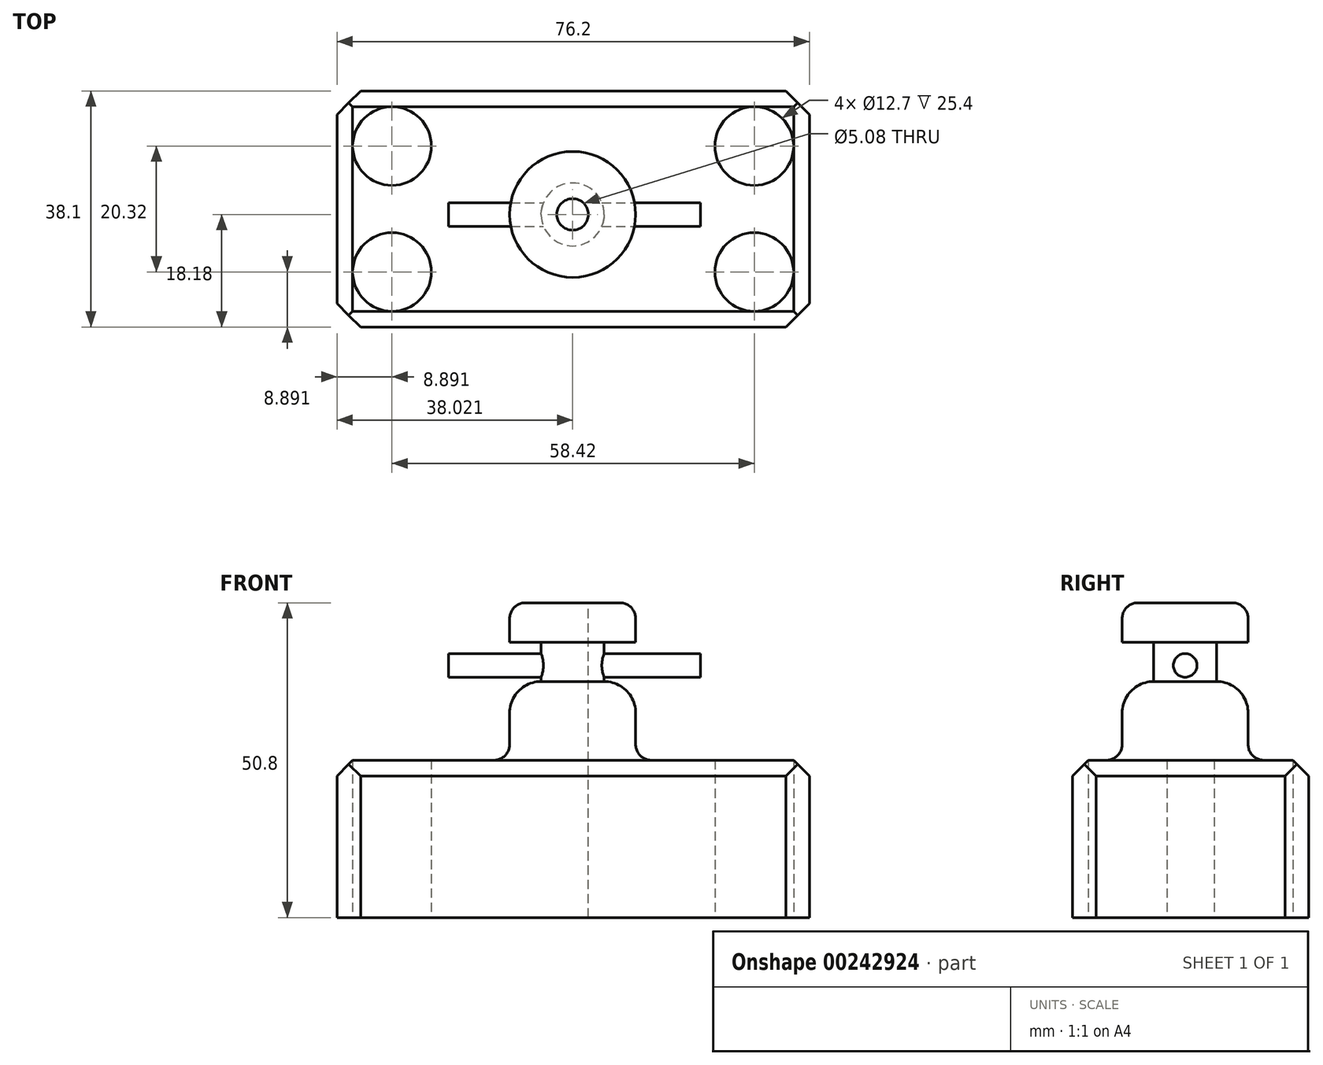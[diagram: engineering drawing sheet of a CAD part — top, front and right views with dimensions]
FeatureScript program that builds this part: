
annotation { "Feature Type Name" : "Feature", "Feature Type Description" : "" }
export const myFeature = defineFeature(function(context is Context, id is Id, definition is map)
    precondition{}
    {
        {
            var Q0;
            Q0=qCreatedBy(makeId("Top.planeOp"),FACE);
            var sketch = newSketch(context, id + "F0", { "sketchPlane" : qUnion([Q0])});
            skLineSegment(sketch, "E0.bottom", {"start": v(-43.42, 19.92) * mm, "end": v(32.78, 19.92) * mm});
            skLineSegment(sketch, "E0.top", {"start": v(-43.42, -18.18) * mm, "end": v(32.78, -18.18) * mm});
            skLineSegment(sketch, "E0.left", {"start": v(-43.42, 19.92) * mm, "end": v(-43.42, -18.18) * mm});
            skLineSegment(sketch, "E0.right", {"start": v(32.78, 19.92) * mm, "end": v(32.78, -18.18) * mm});
            skSolve(sketch);
        }
        {
            var Q0;
            Q0=makeQuery(id+"F0.imprint","IMPRINT",FACE,{"disambiguationData":[TD([[makeQuery(id+"F0.imprint","IMPRINT",EDGE,{"derivedFrom":sQuery(id+"F0.wireOp",EDGE,"E0.bottom")}),-1.0]])]});
            extrude(context, id + "F1", {"entities" : qUnion([Q0]), "depth" : 25.4 * mm});
        }
        {
            var Q0;
            Q0=qCreatedBy(makeId("Top.planeOp"),FACE);
            var sketch = newSketch(context, id + "F2", { "sketchPlane" : qUnion([Q0])});
            skCircle(sketch, "E1", {"center": v(-34.53, -9.29) * mm, "radius": 6.35 * mm});
            skCircle(sketch, "E2", {"center": v(23.9, 11.03) * mm, "radius": 6.35 * mm});
            skCircle(sketch, "E3", {"center": v(23.9, -9.29) * mm, "radius": 6.35 * mm});
            skCircle(sketch, "E4", {"center": v(-34.53, 11.03) * mm, "radius": 6.35 * mm});
            skSolve(sketch);
        }
        {
            var Q0;
            Q0 = qSketchRegion(id + "F2", true);
            var Q1;
            Q1=makeQuery(id+"F1.opExtrude","CAP_FACE",FACE,{"disambiguationData":[OSD([sQuery(id+"F0.wireOp",EDGE,"E0.bottom"),sQuery(id+"F0.wireOp",EDGE,"E0.top"),sQuery(id+"F0.wireOp",EDGE,"E0.left"),sQuery(id+"F0.wireOp",EDGE,"E0.right")])],"isStart":false});
            extrude(context, id + "F3", {"entities" : qUnion([Q0, Q1]), "operationType" : NewBodyOperationType.REMOVE, "depth" : 25.4 * mm});
        }
        {
            var Q0;
            Q0=makeQuery(id+"F1.opExtrude","CAP_EDGE",EDGE,{"disambiguationData":[OSD([sQuery(id+"F0.wireOp",EDGE,"E0.top")])],"isStart":false});
            var Q1;
            Q1=makeQuery(id+"F1.opExtrude","CAP_EDGE",EDGE,{"disambiguationData":[OSD([sQuery(id+"F0.wireOp",EDGE,"E0.right")])],"isStart":false});
            var Q2;
            Q2=makeQuery(id+"F1.opExtrude","CAP_EDGE",EDGE,{"disambiguationData":[OSD([sQuery(id+"F0.wireOp",EDGE,"E0.bottom")])],"isStart":false});
            var Q3;
            Q3=makeQuery(id+"F1.opExtrude","CAP_EDGE",EDGE,{"disambiguationData":[OSD([sQuery(id+"F0.wireOp",EDGE,"E0.left")])],"isStart":false});
            chamfer(context, id + "F4", {"entities" : qUnion([Q0, Q1, Q2, Q3]), "width" : 2.54 * mm, "tangentPropagation" : true});
        }
        {
            var Q0;
            Q0=qCreatedBy(makeId("Top.planeOp"),FACE);
            var sketch = newSketch(context, id + "F5", { "sketchPlane" : qUnion([Q0])});
            skLineSegment(sketch, "E5", {"start": v(32.7, 0) * mm, "end": v(-5.4, 0) * mm});
            skCircle(sketch, "E6", {"center": v(-5.4, 0) * mm, "radius": 10.16 * mm});
            skSolve(sketch);
        }
        {
            var Q0;
            Q0 = qSketchRegion(id + "F5", true);
            extrude(context, id + "F6", {"entities" : qUnion([Q0]), "operationType" : NewBodyOperationType.ADD, "depth" : 38.1 * mm});
        }
        {
            var Q0;
            Q0=makeQuery(id+"F6.opExtrude","CAP_FACE",FACE,{"disambiguationData":[OSD([sQuery(id+"F5.wireOp",EDGE,"E6")])],"isStart":false});
            var sketch = newSketch(context, id + "F7", { "sketchPlane" : qUnion([Q0])});
            skCircle(sketch, "E7", {"center": v(-5.4, 0) * mm, "radius": 5.08 * mm});
            skSolve(sketch);
        }
        {
            var Q0;
            Q0 = qSketchRegion(id + "F7", true);
            extrude(context, id + "F8", {"entities" : qUnion([Q0]), "operationType" : NewBodyOperationType.ADD, "depth" : 6.35 * mm});
        }
        {
            var Q0;
            Q0=makeQuery(id+"F8.opExtrude","CAP_FACE",FACE,{"disambiguationData":[OSD([sQuery(id+"F7.wireOp",EDGE,"E7")])],"isStart":false});
            var sketch = newSketch(context, id + "F9", { "sketchPlane" : qUnion([Q0])});
            skCircle(sketch, "E8", {"center": v(-5.4, 0) * mm, "radius": 10.16 * mm});
            skSolve(sketch);
        }
        {
            var Q0;
            Q0 = qSketchRegion(id + "F9", true);
            extrude(context, id + "F10", {"entities" : qUnion([Q0]), "operationType" : NewBodyOperationType.ADD, "depth" : 6.35 * mm});
        }
        {
            var Q0;
            Q0=qCreatedBy(makeId("Right.planeOp"),FACE);
            var sketch = newSketch(context, id + "F11", { "sketchPlane" : qUnion([Q0])});
            skCircle(sketch, "E9", {"center": v(0, 40.7) * mm, "radius": 1.9 * mm});
            skSolve(sketch);
        }
        {
            var Q0;
            Q0 = qSketchRegion(id + "F11", true);
            extrude(context, id + "F12", {"entities" : qUnion([Q0]), "operationType" : NewBodyOperationType.ADD, "oppositeDirection" : true, "depth" : 25.4 * mm});
        }
        {
            var Q0;
            Q0 = qSketchRegion(id + "F11", true);
            extrude(context, id + "F13", {"entities" : qUnion([Q0]), "operationType" : NewBodyOperationType.ADD, "depth" : 15.24 * mm});
        }
        {
            var Q0;
            Q0=makeQuery(id+"F6.boolean.opBoolean","INTERSECT",EDGE,{"derivedFrom":[makeQuery(id+"F4.opChamfer","SPLIT",FACE,{"disambiguationData":[OD(4.0)],"derivedFrom":makeQuery(id+"F1.opExtrude","CAP_FACE",FACE,{"disambiguationData":[OSD([sQuery(id+"F0.wireOp",EDGE,"E0.bottom"),sQuery(id+"F0.wireOp",EDGE,"E0.top"),sQuery(id+"F0.wireOp",EDGE,"E0.left"),sQuery(id+"F0.wireOp",EDGE,"E0.right")])],"isStart":false})}),makeQuery(id+"F6.opExtrude","SWEPT_FACE",FACE,{"disambiguationData":[OSD([sQuery(id+"F5.wireOp",EDGE,"E6")])]})]});
            fillet(context, id + "F14", {"entities" : qUnion([Q0]), "radius" : 2.54 * mm, "tangentPropagation" : true, "allowEdgeOverflow" : false});
        }
        {
            var Q0;
            Q0=makeQuery(id+"F10.opExtrude","CAP_EDGE",EDGE,{"disambiguationData":[OSD([sQuery(id+"F9.wireOp",EDGE,"E8")])],"isStart":false});
            fillet(context, id + "F15", {"entities" : qUnion([Q0]), "radius" : 2.54 * mm, "tangentPropagation" : true, "allowEdgeOverflow" : false});
        }
        {
            var Q0;
            Q0=makeQuery(id+"F10.opExtrude","CAP_FACE",FACE,{"disambiguationData":[OSD([sQuery(id+"F9.wireOp",EDGE,"E8")])],"isStart":false});
            var sketch = newSketch(context, id + "F16", { "sketchPlane" : qUnion([Q0])});
            skCircle(sketch, "E10", {"center": v(-5.4, 0) * mm, "radius": 2.54 * mm});
            skSolve(sketch);
        }
        {
            var Q0;
            Q0 = qSketchRegion(id + "F16", true);
            extrude(context, id + "F17", {"entities" : qUnion([Q0]), "operationType" : NewBodyOperationType.REMOVE, "oppositeDirection" : true, "depth" : 50.8 * mm});
        }
        {
            var Q0;
            Q0=makeQuery(id+"F1.opExtrude","SWEPT_EDGE",EDGE,{"disambiguationData":[OSD([sQuery(id+"F0.wireOp",EDGE,"E0.top"),sQuery(id+"F0.wireOp",EDGE,"E0.right")])]});
            var Q1;
            Q1=makeQuery(id+"F1.opExtrude","SWEPT_EDGE",EDGE,{"disambiguationData":[OSD([sQuery(id+"F0.wireOp",EDGE,"E0.top"),sQuery(id+"F0.wireOp",EDGE,"E0.left")])]});
            var Q2;
            Q2=makeQuery(id+"F1.opExtrude","SWEPT_EDGE",EDGE,{"disambiguationData":[OSD([sQuery(id+"F0.wireOp",EDGE,"E0.bottom"),sQuery(id+"F0.wireOp",EDGE,"E0.right")])]});
            var Q3;
            Q3=makeQuery(id+"F1.opExtrude","SWEPT_EDGE",EDGE,{"disambiguationData":[OSD([sQuery(id+"F0.wireOp",EDGE,"E0.bottom"),sQuery(id+"F0.wireOp",EDGE,"E0.left")])]});
            chamfer(context, id + "F18", {"entities" : qUnion([Q0, Q1, Q2, Q3]), "width" : 3.8 * mm, "tangentPropagation" : true});
        }
        {
            var Q0;
            Q0=makeQuery(id+"F6.opExtrude","CAP_EDGE",EDGE,{"disambiguationData":[OSD([sQuery(id+"F5.wireOp",EDGE,"E6")])],"isStart":false});
            fillet(context, id + "F19", {"entities" : qUnion([Q0]), "radius" : 5.08 * mm, "tangentPropagation" : true, "allowEdgeOverflow" : false});
        }
    });
